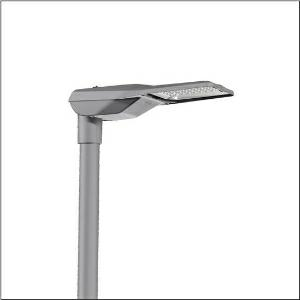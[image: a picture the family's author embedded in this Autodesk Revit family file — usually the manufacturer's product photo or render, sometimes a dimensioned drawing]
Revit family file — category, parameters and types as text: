
# Revit family: streetlight_sl_21_mini___st0_8a_5xe2c33s08jb_c287
name_source: partatom
category: Lighting Fixtures
units: mm (PartAtom-declared; Revit-internal decimal feet)

## family parameters
Cut with Voids When Loaded = No
Host = Face
Light Source = No
Part Type = Normal
Room Calculation Point = No
Round Connector Dimension = Use Diameter
Shared = No

## types (1)
- --- (1 x LED, 12940 lm, 88.6 W, 3000K)
    Apparent Load = 89 VA
    CIE Flux Codes = 41 75 97 100 100
    Color Rendering = 70
    Color Temperature = 3000K
    Default Elevation = 1800 mm
    Description = Streetlight SL 21 mini, mast luminaire, primary light control with lens, of PMMA, primary optical cover: cover, of toughened safety glass, transparent, light distribution: ST0.8a, light emission: direct distribution, primary light characteristic: asymmetric, installation type: side-entry, post-top, LED, High Power LED, rated luminous flux: 12.940lm, luminous efficacy: 146lm/W, light colour: 730, colour temperature: 3000K, control gear: D4i, control: overheat protection, constant luminous flux control, time-dependent luminous flux control, flexible luminous flux parameterisation, pre-setting: logarithmic dimming characteristic, mains connection: 220..240V, AC, 50/60Hz, start of lifetime: 89W, end of service life: 92W, reduction: 41W, luminaire housing, of diecast aluminium, powder-coated, Siteco® metallic grey (DB 702S), corrosivity category C5 mid according to DIN EN ISO 12944, please order mast flange separately, inclination adjustable: 0°, 5°, 10°, 15°, sealing non-destructively replaceable, multi-level sealing system, length: 628mm, width: 235mm, height: 110mm, mast flange for spigot size: 42mm (side-entry): 5XC10008XM4, 60/48mm (side-entry/post-top): 5XC10108XM2, 76/60mm (side-entry/post-top): 5XC10108XM1, mounting height: 4..8m, Smart Interface above, protection rating (complete): IP66, insulation class (complete): insulation class II (safety insulation), certification: CE, ENEC, ENEC+, VDE, impact resistance: IK10, permissible operating ambient temperature for outdoor applications: -40..+50°C, standard-compliant lighting for roads and squares, packaging unit: 1 piece

Light Distribution: ST0.8a
    Height = 110 mm
    Lamp = 1 x LED
    Lamp Light Flux = 12940 lm
    Lamp Power = 88.6 W
    Lamp count = 1
    Length = 625 mm
    Luminous efficacy = 146 lm/W
    Manufacturer = Siteco
    ModVariant = No
    Model = 5XE2C33S08JB
    Number of Poles = 1
    OnlyDefault = Yes
    Power Factor = 1
    Product Name = Streetlight SL 21 mini | ST0.8a
    Product group = mast luminaire | pylon top
    ProductGroupID = 6100
    Protection Class = Protection class II
    Protection Degree = IP 66
    RLX_Detail_Level = 1
    RLX_Emergency_Light_Flux = 0 lm
    RLX_Emergency_Type = 0
    RLX_Emergency_Type_DB = No
    RlxData = <blob elided: 26205 chars, md5=f9a98ed9>
    Socket = socket
    Standby Power = 0 W
    System Light Flux = 12940 lm
    System Power = 89 W
    Type Comments = factory setting: luminous flux: 100 % | dim-lin: 254 | 915 mA
    Type Image = l_1003515.jpg
    URL = http://relux.com
    VarID = @adj_011149
    Voltage = 0 V
    Weight = 0.00 kg
    Width = 234 mm

## geometry (parser evidence)
native form markers: Blend x4, Sweep x9
no freeform markers — native parametric forms only
